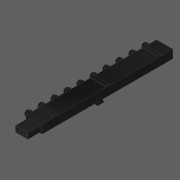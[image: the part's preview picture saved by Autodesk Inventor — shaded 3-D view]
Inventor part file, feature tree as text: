
AUTODESK INVENTOR PART (.ipt)
format: ipt  version: 2020 (Build 240168000, 168)  size: 435,712 bytes
history: native  units: in
note: dims shown in document units (in); Inventor stores cm internally (conversion verified against a paired STEP export)
features: other x8, extrude x5, pattern_linear x2, loft x1, projected_geometry x1, sketch x1
ambient origin geometry x8: Origin, YZ Plane, XZ Plane, XY Plane, X Axis, Y Axis, Z Axis, Center Point
bodies: Solid1 (feature_tree)
feature tree (18):
  other  "CrossSection1"
  other  "Box Sketch"
  extrude  "Box"  Depth=0.5906in
  other  "Fitting Plane"
  other  "Fitting"
  loft  "Fitting Entrance Loft"
  pattern_linear  "Channel Repetition"  Spacing1=0.0in  [1 undecoded]
  extrude  "Small Tabs"  Depth=0.5906in
  extrude  "Big Tabs"  Depth=0.5906in
  extrude  "Connector"  Depth=0.5906in
  pattern_linear  "Connector Fitting Entrance"  Spacing1=0.0492in  [1 undecoded]
  extrude  "End Cap"  Depth=0.5906in
  other  "Fitting Sketch"
  other  "Fitting Entrance Loft From"
  projected_geometry  "Projected Loop1"
  other  "Tab Sketch"
  other  "Fitting Entrance Loft To"
  sketch  "Sketch8"  dims[d0=0.1181in d2=0.0787in d3=0.0787in d7=0.0in d8=0.251in d10=0.0787in d11=0.0197in d12=0.0492in d13=0.0315in d14=0.0938in d15=0.1528in d16=90.0deg d31=0.5906in d32=0.0in d33=0.4872in d34=0.107in d35=0.0619in d36=0.0591in d37=0.107in d38=0.0619in d39=0.0591in d40=0.107in d41=0.0619in d42=0.0591in d49=1.8898in d50=1.8898in d77=0.0295in d79=0.3056in d80=0.0079in d81=0.0079in d82=0.0079in d83=0.0787in d84=0.1299in d85=0.0669in d106=0.4724in d107=0.0in d108=0.1481in d109=0.1528in d110=0.251in d111=0.1245in d113=0.0in d114=90.0deg d115=0.0in d116=90.0deg d117=0.0197in d118=0.0787in d119=-0.125in d120=0.7874in d121=0.7874in d123=0.4724in d124=0.0591in d125=0.0in d128=0.2362in d129=0.1181in d130=0.1181in d131=2.1407in d138=0.5906in d139=0.0in d141=0.0492in d142=0.0492in d9=0.0344in d126=0.0197in d127=0.0344in]
note: 2 required parameter values undecoded (feature->parameter linkage not recoverable at this tier; creation-order binding heuristic only, values carry confidence <= 0.55)
